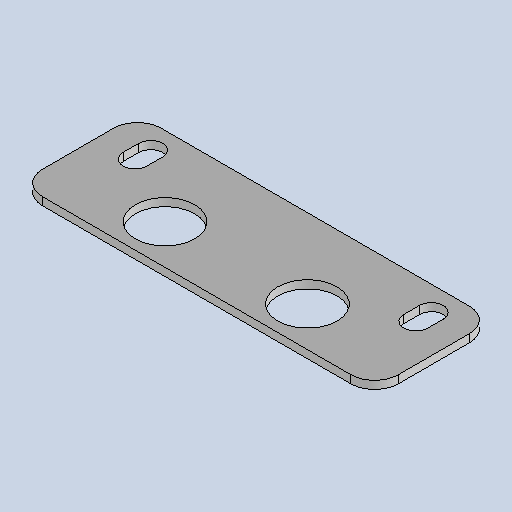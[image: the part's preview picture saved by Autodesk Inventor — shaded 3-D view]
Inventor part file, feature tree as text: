
AUTODESK INVENTOR PART (.ipt)
format: ipt  version: 2025.3 (Build 293356030, 356C)  size: 167,424 bytes
history: native  units: mm
features: other x2, sheet_metal_op x1, chamfer x1, sketch x1
ambient origin geometry x8: Origin, YZ Plane, XZ Plane, XY Plane, X Axis, Y Axis, Z Axis, Center Point
bodies: Solid1 (feature_tree)
feature tree (5):
  sheet_metal_op  "Face1"
  chamfer  "Corner Round1"
  sketch  "Sketch1"  dims[d0=90.0mm d1=30.0mm d2=15.0mm d3=36.0mm d4=2.0mm d5=6.0mm d6=10.0mm d7=6.0mm d8=4.0mm d9=71.0mm]
  other  "Plate1"
  other  "Definition1"
